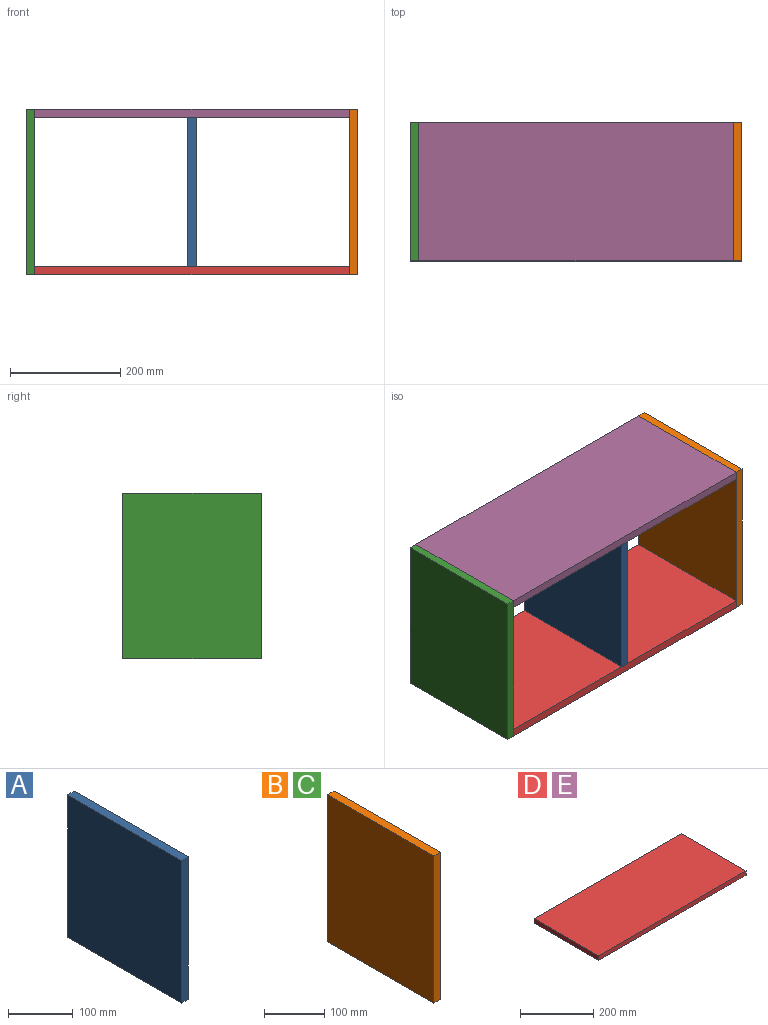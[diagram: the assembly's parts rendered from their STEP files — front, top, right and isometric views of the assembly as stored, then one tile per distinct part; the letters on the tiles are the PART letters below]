
ASSEMBLY  parts=5 mates=4
PART A: 6 faces, bbox 15x250x270 mm
  f0: plane 250x15mm, normal (0,0,1), area 3750mm2, adj f1,f3,f4,f5
  f1: plane 270x15mm, normal (0,-1,0), area 4050mm2, adj f0,f2,f4,f5
  f2: plane 250x15mm, normal (0,0,-1), area 3750mm2, adj f1,f3,f4,f5
  f3: plane 270x15mm, normal (0,1,0), area 4050mm2, adj f0,f2,f4,f5
  f4: plane 270x250mm, normal (1,0,0), area 67500mm2, adj f0,f1,f2,f3
  f5: plane 270x250mm, normal (-1,0,0), area 67500mm2, adj f0,f1,f2,f3
PART B: 6 faces, bbox 15x250x300 mm
  f0: plane 250x15mm, normal (0,0,1), area 3750mm2, adj f1,f3,f4,f5
  f1: plane 300x15mm, normal (0,-1,0), area 4500mm2, adj f0,f2,f4,f5
  f2: plane 250x15mm, normal (0,0,-1), area 3750mm2, adj f1,f3,f4,f5
  f3: plane 300x15mm, normal (0,1,0), area 4500mm2, adj f0,f2,f4,f5
  f4: plane 300x250mm, normal (1,0,0), area 75000mm2, adj f0,f1,f2,f3
  f5: plane 300x250mm, normal (-1,0,0), area 75000mm2, adj f0,f1,f2,f3
PART C: same geometry as B
PART D: 6 faces, bbox 570x250x15 mm
  f0: plane 570x15mm, normal (0,1,0), area 8550mm2, adj f1,f3,f4,f5
  f1: plane 250x15mm, normal (-1,0,0), area 3750mm2, adj f0,f2,f4,f5
  f2: plane 570x15mm, normal (0,-1,0), area 8550mm2, adj f1,f3,f4,f5
  f3: plane 250x15mm, normal (1,0,0), area 3750mm2, adj f0,f2,f4,f5
  f4: plane 570x250mm, normal (0,0,1), area 142500mm2, adj f0,f1,f2,f3
  f5: plane 570x250mm, normal (0,0,-1), area 142500mm2, adj f0,f1,f2,f3
PART E: same geometry as D
PLACE A t=(-206.32,27.04,-6.89)mm
PLACE B t=(86.18,27.04,-21.89)mm
PLACE C t=(-498.82,27.04,-21.89)mm
PLACE D t=(59.35,-113.74,-138.8)mm
PLACE E t=(59.35,-113.74,146.2)mm
MATE fastened C.f1 <-> E.f2  axis (0,-1,0) through (-483.82,-128.66,161.2)mm
MATE fastened D.f2 <-> C.f1  axis (0,-1,0) through (-483.82,-128.66,-138.8)mm
MATE fastened A.f1 <-> E.f2  axis (0,-1,0) through (-198.82,-128.66,146.2)mm
MATE fastened B.f1 <-> E.f2  axis (0,-1,0) through (86.18,-128.66,161.2)mm
